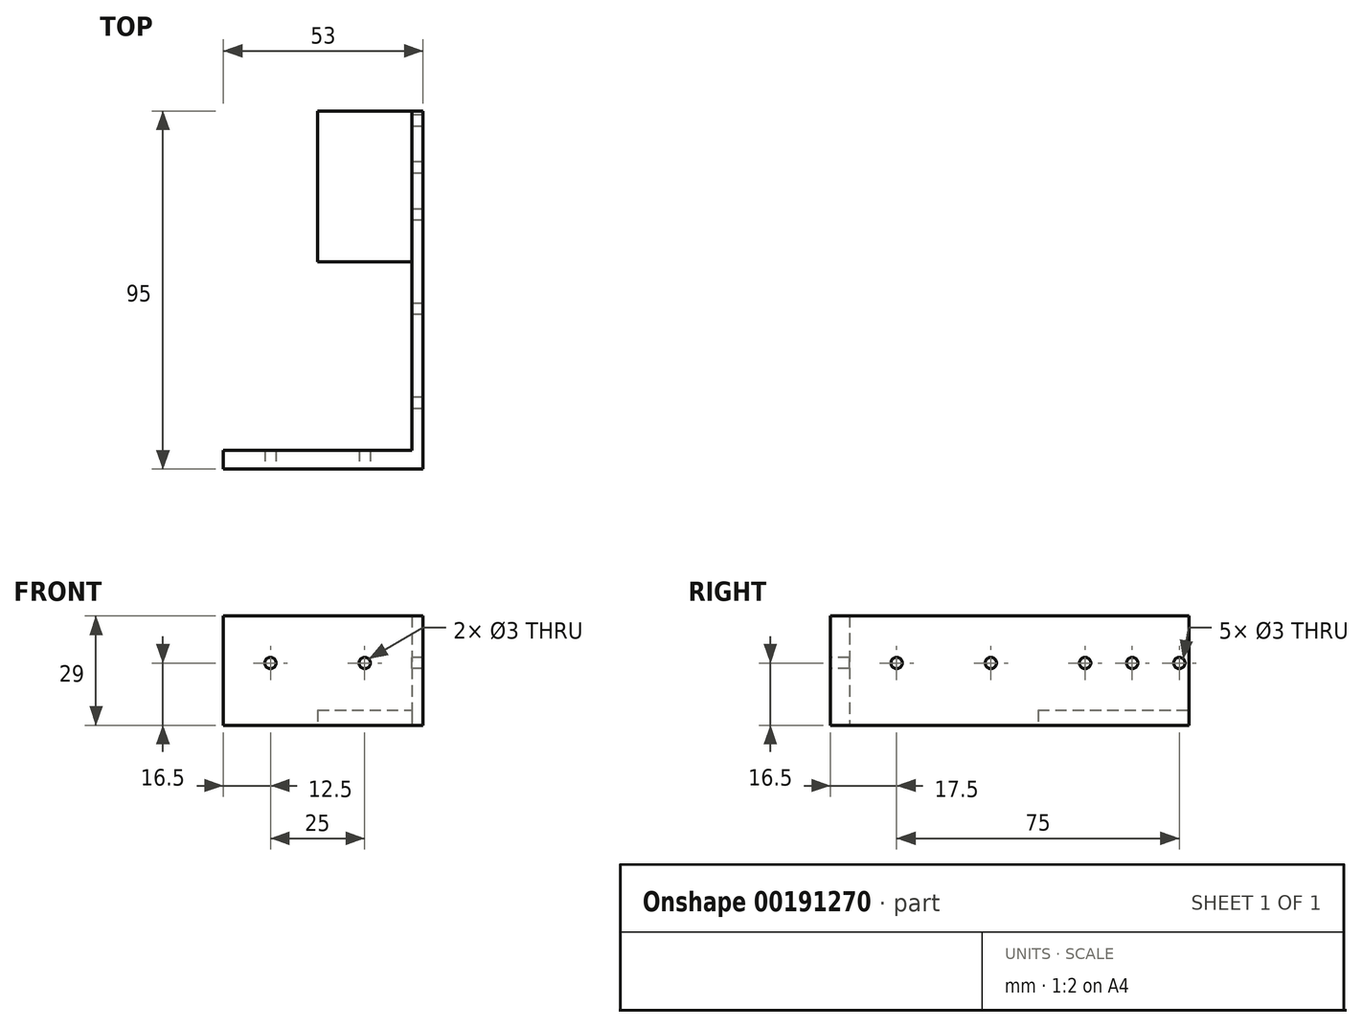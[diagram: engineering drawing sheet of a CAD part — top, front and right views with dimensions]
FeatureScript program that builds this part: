
annotation { "Feature Type Name" : "Feature", "Feature Type Description" : "" }
export const myFeature = defineFeature(function(context is Context, id is Id, definition is map)
    precondition{}
    {
        {
            var Q0;
            Q0=qCreatedBy(makeId("Right.planeOp"),FACE);
            var sketch = newSketch(context, id + "F0", { "sketchPlane" : qUnion([Q0])});
            skLineSegment(sketch, "E0.bottom", {"start": v(-45, 4) * mm, "end": v(45, 4) * mm});
            skLineSegment(sketch, "E0.top", {"start": v(-45, 0) * mm, "end": v(45, 0) * mm});
            skLineSegment(sketch, "E0.left", {"start": v(-45, 4) * mm, "end": v(-45, 0) * mm});
            skLineSegment(sketch, "E0.right", {"start": v(45, 4) * mm, "end": v(45, 0) * mm});
            skLineSegment(sketch, "E1", {"start": v(-45, 4) * mm, "end": v(-45, 29) * mm});
            skLineSegment(sketch, "E2", {"start": v(-45, 29) * mm, "end": v(45, 29) * mm});
            skLineSegment(sketch, "E3", {"start": v(45, 29) * mm, "end": v(45, 4) * mm});
            skLineSegment(sketch, "E4.0", {"start": v(-32.5, 4) * mm, "end": v(-32.5, 29) * mm, "construction": true});
            skLineSegment(sketch, "E5.0", {"start": v(-7.5, 4) * mm, "end": v(-7.5, 29) * mm, "construction": true});
            skLineSegment(sketch, "E6.0", {"start": v(17.5, 4) * mm, "end": v(17.5, 29) * mm, "construction": true});
            skLineSegment(sketch, "E7.0", {"start": v(42.5, 4) * mm, "end": v(42.5, 29) * mm, "construction": true});
            skLineSegment(sketch, "E8.0", {"start": v(30, 4) * mm, "end": v(30, 29) * mm, "construction": true});
            skCircle(sketch, "E9", {"center": v(-32.5, 16.5) * mm, "radius": 1.5 * mm});
            skCircle(sketch, "E10", {"center": v(-7.5, 16.5) * mm, "radius": 1.5 * mm});
            skCircle(sketch, "E11", {"center": v(17.5, 16.5) * mm, "radius": 1.5 * mm});
            skCircle(sketch, "E12", {"center": v(30, 16.5) * mm, "radius": 1.5 * mm});
            skCircle(sketch, "E13", {"center": v(42.5, 16.5) * mm, "radius": 1.5 * mm});
            skLineSegment(sketch, "E14.0", {"start": v(-50, 0) * mm, "end": v(-50, 29) * mm});
            skLineSegment(sketch, "E15", {"start": v(-45, 0) * mm, "end": v(-50, 0) * mm});
            skLineSegment(sketch, "E16", {"start": v(-45, 29) * mm, "end": v(-50, 29) * mm});
            skLineSegment(sketch, "E17.0", {"start": v(5, 4) * mm, "end": v(5, 0) * mm});
            skSolve(sketch);
        }
        {
            var Q0;
            {var subQ0=sQuery(id+"F0.wireOp",EDGE,"E0.left");Q0=makeQuery(id+"F0.imprint","IMPRINT",FACE,{"disambiguationData":[TD([[makeQuery(id+"F0.imprint","IMPRINT",EDGE,{"derivedFrom":subQ0}),1.0]])]});}
            var Q1;
            {var subQ0=sQuery(id+"F0.wireOp",EDGE,"E1");Q1=makeQuery(id+"F0.imprint","IMPRINT",FACE,{"disambiguationData":[TD([[makeQuery(id+"F0.imprint","IMPRINT",EDGE,{"derivedFrom":subQ0}),-1.0]])]});}
            extrude(context, id + "F1", {"entities" : qUnion([Q0, Q1]), "depth" : 3 * mm, "offsetDistance" : 25 * mm});
        }
        {
            var Q0;
            Q0=makeQuery(id+"F0.imprint","IMPRINT",FACE,{"disambiguationData":[TD([[makeQuery(id+"F0.imprint","IMPRINT",EDGE,{"derivedFrom":sQuery(id+"F0.wireOp",EDGE,"E0.left")}),-1.0]])]});
            extrude(context, id + "F2", {"entities" : qUnion([Q0]), "operationType" : NewBodyOperationType.ADD, "oppositeDirection" : true, "depth" : 50 * mm, "offsetDistance" : 25 * mm, "hasSecondDirection" : true, "secondDirectionOppositeDirection" : false, "secondDirectionDepth" : 3 * mm});
        }
        {
            var Q0;
            {var subQ0=sQuery(id+"F0.wireOp",EDGE,"E0.right");Q0=makeQuery(id+"F0.imprint","IMPRINT",FACE,{"disambiguationData":[TD([[makeQuery(id+"F0.imprint","IMPRINT",EDGE,{"derivedFrom":subQ0}),-1.0]])]});}
            extrude(context, id + "F3", {"entities" : qUnion([Q0]), "operationType" : NewBodyOperationType.ADD, "oppositeDirection" : true, "depth" : 25 * mm, "offsetDistance" : 25 * mm, "hasSecondDirection" : true, "secondDirectionOppositeDirection" : false, "secondDirectionDepth" : 3 * mm});
        }
        {
            var Q0;
            Q0=makeQuery(id+"F2.opExtrude","SWEPT_FACE",FACE,{"disambiguationData":[OSD([sQuery(id+"F0.wireOp",EDGE,"E14.0")])]});
            var sketch = newSketch(context, id + "F4", { "sketchPlane" : qUnion([Q0])});
            skLineSegment(sketch, "E18.0", {"start": v(-37.5, 0) * mm, "end": v(-37.5, 29) * mm, "construction": true});
            skLineSegment(sketch, "E19.0", {"start": v(-12.5, 0) * mm, "end": v(-12.5, 29) * mm, "construction": true});
            skCircle(sketch, "E20", {"center": v(-37.5, 16.5) * mm, "radius": 1.5 * mm});
            skCircle(sketch, "E21", {"center": v(-12.5, 16.5) * mm, "radius": 1.5 * mm});
            skSolve(sketch);
        }
        {
            var Q0;
            Q0=makeQuery(id+"F4.imprint","IMPRINT",FACE,{"disambiguationData":[TD([[makeQuery(id+"F4.imprint","IMPRINT",EDGE,{"derivedFrom":sQuery(id+"F4.wireOp",EDGE,"E20")}),1.0]])]});
            var Q1;
            Q1=makeQuery(id+"F4.imprint","IMPRINT",FACE,{"disambiguationData":[TD([[makeQuery(id+"F4.imprint","IMPRINT",EDGE,{"derivedFrom":sQuery(id+"F4.wireOp",EDGE,"E21")}),1.0]])]});
            extrude(context, id + "F5", {"entities" : qUnion([Q0, Q1]), "operationType" : NewBodyOperationType.REMOVE, "oppositeDirection" : true, "depth" : 25 * mm, "offsetDistance" : 25 * mm});
        }
    });
